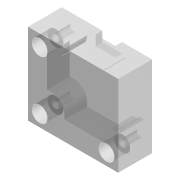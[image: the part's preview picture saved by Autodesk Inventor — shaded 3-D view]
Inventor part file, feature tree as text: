
AUTODESK INVENTOR PART (.ipt)
format: ipt  version: 2015 SP1 (Build 190203100, 203)  size: 251,392 bytes
history: native  units: mm
features: extrude x6, sketch x3, other x1
ambient origin geometry x8: Origin, YZ Plane, XZ Plane, XY Plane, X Axis, Y Axis, Z Axis, Center Point
bodies: Body1 (feature_tree)
feature tree (10):
  other  "Твердое тело1"
  extrude  "Выдавливание1"  Depth=36.0mm
  extrude  "Выдавливание2"  Depth=32.0mm
  extrude  "Выдавливание3"  Depth=3.18mm
  extrude  "Выдавливание5"  Depth=3.18mm
  extrude  "Выдавливание6"  Depth=3.18mm
  extrude  "Выдавливание7"  Depth=3.18mm
  sketch  "Эскиз2"
  sketch  "Эскиз3"
  sketch  "Эскиз4"
